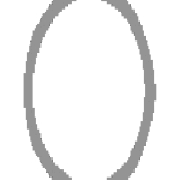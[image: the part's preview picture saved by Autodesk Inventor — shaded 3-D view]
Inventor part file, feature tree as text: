
AUTODESK INVENTOR PART (.ipt)
format: ipt  version: 2021 (Build 250183000, 183)  size: 109,568 bytes
history: native  units: in
note: dims shown in document units (in); Inventor stores cm internally (conversion verified against a paired STEP export)
features: other x4, sketch x3, plane x1
ambient origin geometry x8: Origin, YZ Plane, XZ Plane, XY Plane, X Axis, Y Axis, Z Axis, Center Point
bodies: Solid1 (feature_tree), Body (feature_tree)
feature tree (8):
  other  "Driven Length"
  other  "Frame Generator"
  other  "Start Plane"
  other  "End Plane"
  sketch  "Sketch"  dims[d2=19.5707in d4=-0.0in d5=19.5707in d6=0.12in d7=0.0in d8=90.0deg d9=19.5707in]
  sketch  "Sketch2"  dims[d0=1.0in]
  plane  "Work Plane3"
  sketch  "Sketch3"  dims[d1=0.065in]
